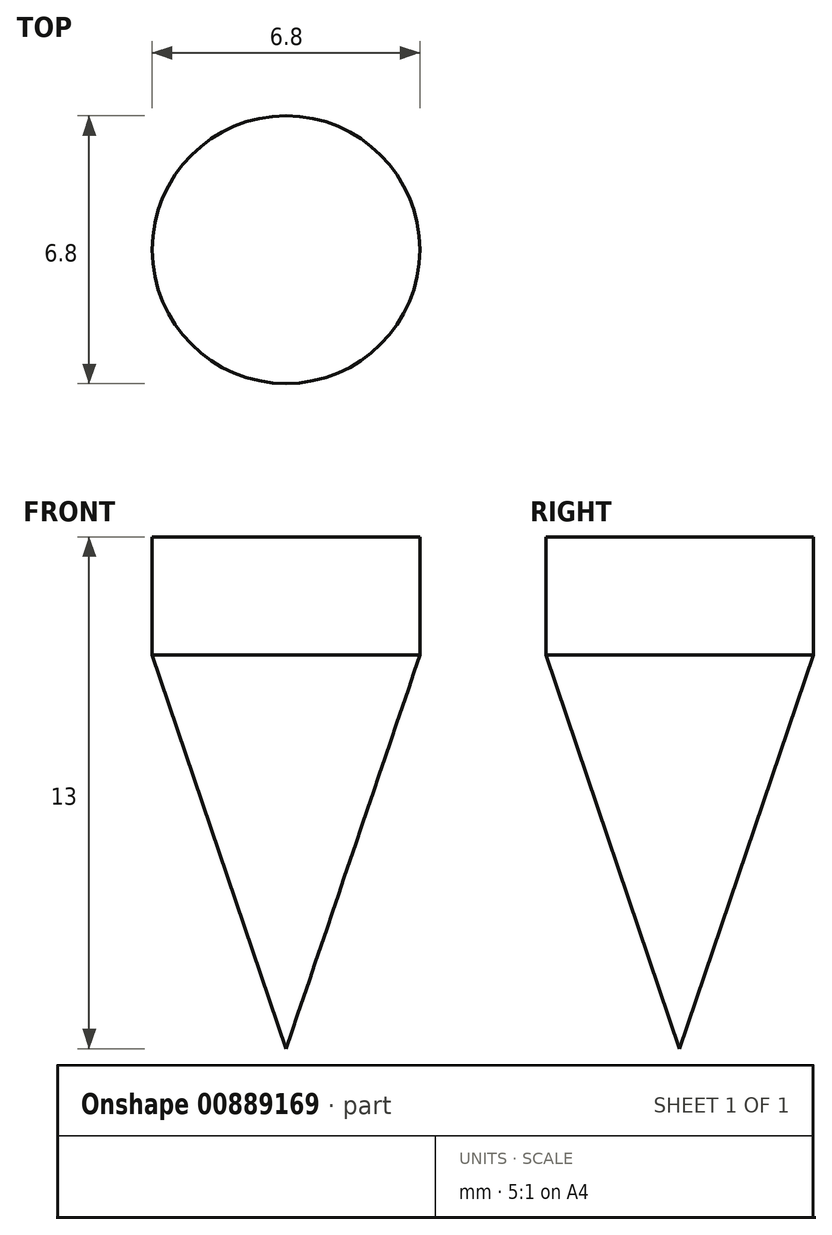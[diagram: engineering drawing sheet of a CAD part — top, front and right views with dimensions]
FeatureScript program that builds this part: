
annotation { "Feature Type Name" : "Feature", "Feature Type Description" : "" }
export const myFeature = defineFeature(function(context is Context, id is Id, definition is map)
    precondition{}
    {
        {
            var Q0;
            Q0=qCreatedBy(makeId("Top.planeOp"),FACE);
            var sketch = newSketch(context, id + "F0", { "sketchPlane" : qUnion([Q0])});
            skCircle(sketch, "E0", {"center": v(0, 0) * mm, "radius": 3.4 * mm});
            skSolve(sketch);
        }
        {
            var Q0;
            Q0 = qSketchRegion(id + "F0", true);
            extrude(context, id + "F1", {"entities" : qUnion([Q0]), "depth" : 3 * mm, "offsetDistance" : 25 * mm});
        }
        {
            var Q0;
            Q0=qCreatedBy(makeId("Front.planeOp"),FACE);
            var sketch = newSketch(context, id + "F2", { "sketchPlane" : qUnion([Q0])});
            skLineSegment(sketch, "E1", {"start": v(-3.4, 0) * mm, "end": v(0, -10) * mm});
            skLineSegment(sketch, "E2", {"start": v(0, -10) * mm, "end": v(0, 0) * mm});
            skLineSegment(sketch, "E3", {"start": v(0, 0) * mm, "end": v(-3.4, 0) * mm});
            skSolve(sketch);
        }
        {
            var Q0;
            Q0 = qSketchRegion(id + "F2", true);
            var Q1;
            Q1=sQuery(id+"F2.wireOp",EDGE,"E2");
            revolve(context, id + "F3", {"operationType" : NewBodyOperationType.ADD, "surfaceOperationType" : NewSurfaceOperationType.NEW, "entities" : qUnion([Q0]), "axis" : qUnion([Q1]), "revolveType" : RevolveType.FULL});
        }
    });
